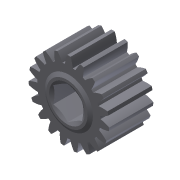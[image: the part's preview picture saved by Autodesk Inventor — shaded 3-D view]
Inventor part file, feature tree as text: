
AUTODESK INVENTOR PART (.ipt)
format: ipt  version: 2013 (Build 170138000, 138)  size: 250,368 bytes
history: native  units: mm (DEFAULTED — no unit token found)
features: sketch x5, extrude x3, plane x3, other x3, revolve x1, projected_geometry x1
ambient origin geometry x8: Origin, YZ Plane, XZ Plane, XY Plane, X Axis, Y Axis, Z Axis, Center Point
bodies: Solid1 (feature_tree)
feature tree (16):
  extrude  "Extrusion1"  Depth=14.605mm TaperAngle=0.0deg
  plane  "Work Plane1"
  plane  "Work Plane2"
  plane  "Work Plane3"
  other  "Spur Gear"
  extrude  "Extrusion2"  Depth=76.2mm TaperAngle=0.0deg
  extrude  "Extrusion3"  Depth=15.9004mm
  revolve  "Revolution1"  [1 undecoded]
  sketch  "Sketch1"  dims[d0=26.67mm d1=14.605mm d2=0.0mm]
  sketch  "Sketch2"  dims[d3=24.13mm d4=76.2mm d5=0.0mm]
  other  "Srf1"
  sketch  "Sketch3"  dims[d6=0.0mm d7=1.65347mm d20=15.9004mm]
  sketch  "Sketch4"  dims[d21=0.635mm d22=0.0mm d23=9.525mm]
  sketch  "Sketch5"  dims[d24=0.635mm d25=0.0mm d26=1.143mm d27=0.889mm d28=5.070181mm d29=2.54mm d30=90.0deg]
  other  "Pitch Diameter"
  projected_geometry  "Project Cut Edges1"
note: 1 required parameter value undecoded (feature->parameter linkage not recoverable at this tier; creation-order binding heuristic only, values carry confidence <= 0.55)
